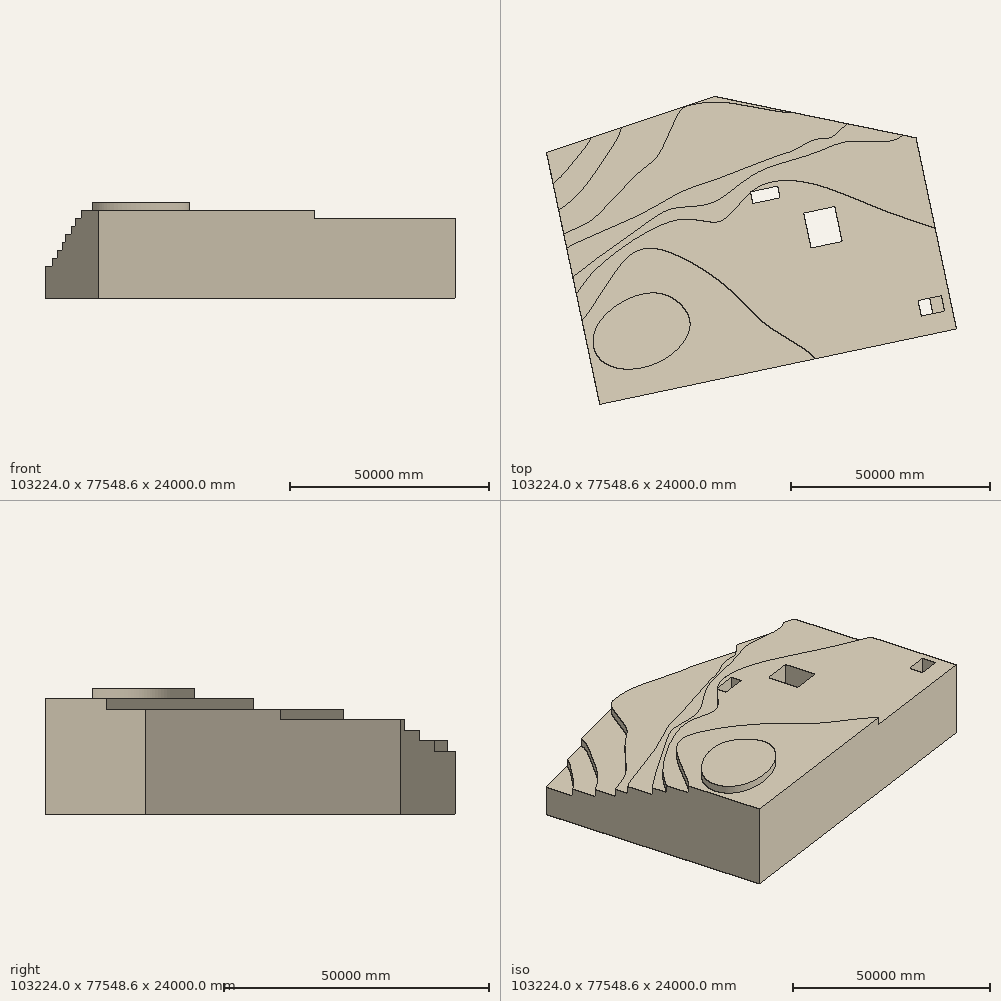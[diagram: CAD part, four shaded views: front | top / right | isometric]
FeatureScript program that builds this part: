
annotation { "Feature Type Name" : "Feature", "Feature Type Description" : "" }
export const myFeature = defineFeature(function(context is Context, id is Id, definition is map)
    precondition{}
    {
        {
            var Q0;
            Q0=qCreatedBy(makeId("Top.planeOp"),FACE);
            var sketch = newSketch(context, id + "F0", { "sketchPlane" : qUnion([Q0])});
            skLineSegment(sketch, "E0.bottom", {"start": v(-42585.65, -35950.06) * mm, "end": v(47226.6, -16950.06) * mm});
            skLineSegment(sketch, "E0.left", {"start": v(-42585.65, -35950.06) * mm, "end": v(-55997.42, 27446.82) * mm});
            skLineSegment(sketch, "E0.right", {"start": v(47226.6, -16950.06) * mm, "end": v(37043.6, 31184.6) * mm});
            skLineSegment(sketch, "E1", {"start": v(-55997.42, 27446.82) * mm, "end": v(-13596.71, 41598.52) * mm});
            skLineSegment(sketch, "E2", {"start": v(-13596.71, 41598.52) * mm, "end": v(37043.6, 31184.6) * mm});
            skSolve(sketch);
        }
        {
            var Q0;
            Q0 = qSketchRegion(id + "F0", true);
            extrude(context, id + "F1", {"entities" : qUnion([Q0]), "oppositeDirection" : true, "depth" : 20000 * mm, "offsetDistance" : 25 * mm});
        }
        {
            var Q0;
            Q0=makeQuery(id+"F1.opExtrude","CAP_FACE",FACE,{"disambiguationData":[OSD([sQuery(id+"F0.wireOp",EDGE,"E0.bottom"),sQuery(id+"F0.wireOp",EDGE,"E0.left"),sQuery(id+"F0.wireOp",EDGE,"E0.right"),sQuery(id+"F0.wireOp",EDGE,"E1"),sQuery(id+"F0.wireOp",EDGE,"E2")])],"isStart":true});
            var sketch = newSketch(context, id + "F2", { "sketchPlane" : qUnion([Q0])});
            skLineSegment(sketch, "E3.bottom", {"start": v(8756.37, 12219.3) * mm, "end": v(16583.14, 13875.07) * mm});
            skLineSegment(sketch, "E3.top", {"start": v(10619.11, 3414.18) * mm, "end": v(18445.89, 5069.95) * mm});
            skLineSegment(sketch, "E3.left", {"start": v(8756.37, 12219.3) * mm, "end": v(10619.11, 3414.18) * mm});
            skLineSegment(sketch, "E3.right", {"start": v(16583.14, 13875.07) * mm, "end": v(18445.89, 5069.95) * mm});
            skSolve(sketch);
        }
        {
            var Q0;
            Q0 = qSketchRegion(id + "F2", true);
            extrude(context, id + "F3", {"entities" : qUnion([Q0]), "operationType" : NewBodyOperationType.REMOVE, "endBound" : BoundingType.THROUGH_ALL, "oppositeDirection" : true, "depth" : 25 * mm, "offsetDistance" : 25 * mm});
        }
        {
            var Q0;
            Q0=makeQuery(id+"F1.opExtrude","CAP_FACE",FACE,{"disambiguationData":[OSD([sQuery(id+"F0.wireOp",EDGE,"E0.bottom"),sQuery(id+"F0.wireOp",EDGE,"E0.left"),sQuery(id+"F0.wireOp",EDGE,"E0.right"),sQuery(id+"F0.wireOp",EDGE,"E1"),sQuery(id+"F0.wireOp",EDGE,"E2")])],"isStart":true});
            var sketch = newSketch(context, id + "F4", { "sketchPlane" : qUnion([Q0])});
            skLineSegment(sketch, "E4.bottom", {"start": v(37537.08, -9800.71) * mm, "end": v(43407.16, -8558.88) * mm});
            skLineSegment(sketch, "E4.top", {"start": v(38364.96, -13714.1) * mm, "end": v(44235.04, -12472.27) * mm});
            skLineSegment(sketch, "E4.left", {"start": v(37537.08, -9800.71) * mm, "end": v(38364.96, -13714.1) * mm});
            skLineSegment(sketch, "E4.right", {"start": v(43407.16, -8558.88) * mm, "end": v(44235.04, -12472.27) * mm});
            skSolve(sketch);
        }
        {
            var Q0;
            Q0 = qSketchRegion(id + "F4", true);
            extrude(context, id + "F5", {"entities" : qUnion([Q0]), "operationType" : NewBodyOperationType.REMOVE, "endBound" : BoundingType.THROUGH_ALL, "oppositeDirection" : true, "depth" : 25 * mm, "offsetDistance" : 25 * mm});
        }
        {
            var Q0;
            Q0=makeQuery(id+"F1.opExtrude","CAP_FACE",FACE,{"disambiguationData":[OSD([sQuery(id+"F0.wireOp",EDGE,"E0.bottom"),sQuery(id+"F0.wireOp",EDGE,"E0.left"),sQuery(id+"F0.wireOp",EDGE,"E0.right"),sQuery(id+"F0.wireOp",EDGE,"E1"),sQuery(id+"F0.wireOp",EDGE,"E2")])],"isStart":true});
            var sketch = newSketch(context, id + "F6", { "sketchPlane" : qUnion([Q0])});
            skLineSegment(sketch, "E5.bottom", {"start": v(-4639.57, 17562.41) * mm, "end": v(2208.86, 19011.22) * mm});
            skLineSegment(sketch, "E5.top", {"start": v(-4018.65, 14627.37) * mm, "end": v(2829.77, 16076.18) * mm});
            skLineSegment(sketch, "E5.left", {"start": v(-4639.57, 17562.41) * mm, "end": v(-4018.65, 14627.37) * mm});
            skLineSegment(sketch, "E5.right", {"start": v(2208.86, 19011.22) * mm, "end": v(2829.77, 16076.18) * mm});
            skSolve(sketch);
        }
        {
            var Q0;
            Q0 = qSketchRegion(id + "F6", true);
            extrude(context, id + "F7", {"entities" : qUnion([Q0]), "operationType" : NewBodyOperationType.REMOVE, "endBound" : BoundingType.THROUGH_ALL, "oppositeDirection" : true, "depth" : 25 * mm, "offsetDistance" : 25 * mm});
        }
        {
            var Q0;
            Q0=makeQuery(id+"F1.opExtrude","CAP_FACE",FACE,{"disambiguationData":[OSD([sQuery(id+"F0.wireOp",EDGE,"E0.bottom"),sQuery(id+"F0.wireOp",EDGE,"E0.left"),sQuery(id+"F0.wireOp",EDGE,"E0.right"),sQuery(id+"F0.wireOp",EDGE,"E1"),sQuery(id+"F0.wireOp",EDGE,"E2")])],"isStart":false});
            var sketch = newSketch(context, id + "F8", { "sketchPlane" : qUnion([Q0])});
            skPoint(sketch, "E6.oppositeSnap0", {"position": v(40472.12, 9179.8) * mm});
            skLineSegment(sketch, "E6.bottom", {"start": v(43407.16, 8558.88) * mm, "end": v(40472.12, 9179.8) * mm});
            skLineSegment(sketch, "E6.top", {"start": v(44235.04, 12472.27) * mm, "end": v(41300, 13093.18) * mm});
            skLineSegment(sketch, "E6.left", {"start": v(43407.16, 8558.88) * mm, "end": v(44235.04, 12472.27) * mm});
            skLineSegment(sketch, "E6.right", {"start": v(40472.12, 9179.8) * mm, "end": v(41300, 13093.18) * mm});
            skSolve(sketch);
        }
        {
            var Q0;
            Q0 = qSketchRegion(id + "F8", true);
            extrude(context, id + "F9", {"entities" : qUnion([Q0]), "operationType" : NewBodyOperationType.ADD, "oppositeDirection" : true, "depth" : 5000 * mm, "offsetDistance" : 25 * mm});
        }
        {
            var Q0;
            Q0=makeQuery(id+"F1.opExtrude","CAP_FACE",FACE,{"disambiguationData":[OSD([sQuery(id+"F0.wireOp",EDGE,"E0.bottom"),sQuery(id+"F0.wireOp",EDGE,"E0.left"),sQuery(id+"F0.wireOp",EDGE,"E0.right"),sQuery(id+"F0.wireOp",EDGE,"E1"),sQuery(id+"F0.wireOp",EDGE,"E2")])],"isStart":true});
            var sketch = newSketch(context, id + "F10", { "sketchPlane" : qUnion([Q0])});
            skFitSpline(sketch, "E7", {"points": [v(-47056.24, -14817.77) * mm, v(-34800.37, 1655.55) * mm, v(-24164.4, 2014.67) * mm, v(-9621.3, -7204.95) * mm, v(-153.95, -16251.36) * mm, v(11663.69, -24473.48) * mm], "startDerivative": vector(45294.7, 43443.74) * mm, "endDerivative": vector(43323.64, -51386.55) * mm});
            skLineSegment(sketch, "E8", {"start": v(-47056.24, -14817.77) * mm, "end": v(-42585.65, -35950.06) * mm});
            skLineSegment(sketch, "E9", {"start": v(-42585.65, -35950.06) * mm, "end": v(11663.69, -24473.48) * mm});
            skSolve(sketch);
        }
        {
            var Q0;
            Q0 = qSketchRegion(id + "F10", true);
            extrude(context, id + "F11", {"entities" : qUnion([Q0]), "operationType" : NewBodyOperationType.ADD, "depth" : 2000 * mm, "offsetDistance" : 25 * mm});
        }
        {
            var Q0;
            Q0=makeQuery(id+"F11.opExtrude","CAP_FACE",FACE,{"disambiguationData":[OSD([sQuery(id+"F10.wireOp",EDGE,"E7"),sQuery(id+"F10.wireOp",EDGE,"E8"),sQuery(id+"F10.wireOp",EDGE,"E9")])],"isStart":false});
            var sketch = newSketch(context, id + "F12", { "sketchPlane" : qUnion([Q0])});
            skFitSpline(sketch, "E10", {"points": [v(-44223.86, -19267.9) * mm, v(-39474.26, -11956.56) * mm, v(-27071.1, -8065.2) * mm, v(-19862.81, -15371.49) * mm, v(-25559.14, -24150.56) * mm, v(-36282.75, -27042.67) * mm, v(-42478.37, -24571.47) * mm, v(-44223.86, -19267.9) * mm]});
            skSolve(sketch);
        }
        {
            var Q0;
            Q0 = qSketchRegion(id + "F12", true);
            extrude(context, id + "F13", {"entities" : qUnion([Q0]), "operationType" : NewBodyOperationType.ADD, "depth" : 2000 * mm, "offsetDistance" : 25 * mm});
        }
        {
            var Q0;
            Q0=makeQuery(id+"F1.opExtrude","CAP_FACE",FACE,{"disambiguationData":[OSD([sQuery(id+"F0.wireOp",EDGE,"E0.bottom"),sQuery(id+"F0.wireOp",EDGE,"E0.left"),sQuery(id+"F0.wireOp",EDGE,"E0.right"),sQuery(id+"F0.wireOp",EDGE,"E1"),sQuery(id+"F0.wireOp",EDGE,"E2")])],"isStart":true});
            var sketch = newSketch(context, id + "F14", { "sketchPlane" : qUnion([Q0])});
            skPoint(sketch, "E11.4.internal.snap0", {"position": v(-2894.94, 18493.67) * mm});
            skPoint(sketch, "E11.5.internal.snap0", {"position": v(2519.32, 17543.7) * mm});
            skFitSpline(sketch, "E11", {"points": [v(-48461.58, -8174.79) * mm, v(-41902.03, -480.55) * mm, v(-22214.21, 10624.74) * mm, v(-12056.5, 10248.96) * mm, v(-3098.95, 18493.67) * mm, v(11165.64, 19577.27) * mm, v(26210.48, 13928.82) * mm, v(41861.9, 8408.7) * mm], "startDerivative": vector(61772.48, 88890.48) * mm, "endDerivative": vector(86929.9, -27804.28) * mm});
            skLineSegment(sketch, "E12", {"start": v(41861.9, 8408.7) * mm, "end": v(37043.6, 31184.6) * mm});
            skLineSegment(sketch, "E13", {"start": v(37043.6, 31184.6) * mm, "end": v(-13596.71, 41598.52) * mm});
            skLineSegment(sketch, "E14", {"start": v(-13596.71, 41598.52) * mm, "end": v(-55997.42, 27446.82) * mm});
            skLineSegment(sketch, "E15", {"start": v(-55997.42, 27446.82) * mm, "end": v(-48461.58, -8174.79) * mm});
            skSolve(sketch);
        }
        {
            var Q0;
            Q0 = qSketchRegion(id + "F14", true);
            extrude(context, id + "F15", {"entities" : qUnion([Q0]), "operationType" : NewBodyOperationType.REMOVE, "oppositeDirection" : true, "depth" : 2000 * mm, "offsetDistance" : 25 * mm});
        }
        {
            var Q0;
            Q0=makeQuery(id+"F15.boolean.opBoolean","COPY",FACE,{"derivedFrom":makeQuery(id+"F15.opExtrude","CAP_FACE",FACE,{"disambiguationData":[OSD([sQuery(id+"F14.wireOp",EDGE,"E11"),sQuery(id+"F14.wireOp",EDGE,"E12"),sQuery(id+"F14.wireOp",EDGE,"E13"),sQuery(id+"F14.wireOp",EDGE,"E14"),sQuery(id+"F14.wireOp",EDGE,"E15")])],"isStart":false})});
            var sketch = newSketch(context, id + "F16", { "sketchPlane" : qUnion([Q0])});
            skFitSpline(sketch, "E16", {"points": [v(-49355.7, -3948.33) * mm, v(-32457.5, 8457.75) * mm, v(-24055.05, 13383.47) * mm, v(-14282.3, 14827.42) * mm, v(-3249.43, 22200.56) * mm, v(10835.35, 27081.4) * mm, v(19620.7, 30197.18) * mm, v(28436.95, 30171.34) * mm, v(33752.23, 31861.46) * mm], "startDerivative": vector(74101.45, 64075.98) * mm, "endDerivative": vector(44716.5, 40997.05) * mm});
            skLineSegment(sketch, "E17", {"start": v(33752.23, 31861.46) * mm, "end": v(-13596.71, 41598.52) * mm});
            skLineSegment(sketch, "E18", {"start": v(-13596.71, 41598.52) * mm, "end": v(-55997.42, 27446.82) * mm});
            skLineSegment(sketch, "E19", {"start": v(-55997.42, 27446.82) * mm, "end": v(-49355.7, -3948.33) * mm});
            skSolve(sketch);
        }
        {
            var Q0;
            Q0 = qSketchRegion(id + "F16", true);
            extrude(context, id + "F17", {"entities" : qUnion([Q0]), "operationType" : NewBodyOperationType.REMOVE, "oppositeDirection" : true, "depth" : 2000 * mm, "offsetDistance" : 25 * mm});
        }
        {
            var Q0;
            Q0=makeQuery(id+"F17.boolean.opBoolean","COPY",FACE,{"derivedFrom":makeQuery(id+"F17.opExtrude","CAP_FACE",FACE,{"disambiguationData":[OSD([sQuery(id+"F16.wireOp",EDGE,"E16"),sQuery(id+"F16.wireOp",EDGE,"E17"),sQuery(id+"F16.wireOp",EDGE,"E18"),sQuery(id+"F16.wireOp",EDGE,"E19")])],"isStart":false})});
            var sketch = newSketch(context, id + "F18", { "sketchPlane" : qUnion([Q0])});
            skFitSpline(sketch, "E20", {"points": [v(-50887.29, 3291.44) * mm, v(-33094.98, 11471.05) * mm, v(-21809.6, 17650.61) * mm, v(-13024.26, 20766.4) * mm, v(934.27, 26244.03) * mm, v(6226, 27997.22) * mm, v(11943.66, 30780.9) * mm, v(15617.92, 31241.33) * mm, v(19924.26, 34705.1) * mm], "startDerivative": vector(49233.01, 38234.62) * mm, "endDerivative": vector(82012.7, 60654.18) * mm});
            skLineSegment(sketch, "E21", {"start": v(19924.26, 34705.1) * mm, "end": v(-13596.71, 41598.52) * mm});
            skLineSegment(sketch, "E22", {"start": v(-13596.71, 41598.52) * mm, "end": v(-55997.42, 27446.82) * mm});
            skLineSegment(sketch, "E23", {"start": v(-55997.42, 27446.82) * mm, "end": v(-50887.29, 3291.44) * mm});
            skSolve(sketch);
        }
        {
            var Q0;
            Q0 = qSketchRegion(id + "F18", true);
            extrude(context, id + "F19", {"entities" : qUnion([Q0]), "operationType" : NewBodyOperationType.REMOVE, "oppositeDirection" : true, "depth" : 2000 * mm, "offsetDistance" : 25 * mm});
        }
        {
            var Q0;
            Q0=makeQuery(id+"F19.boolean.opBoolean","COPY",FACE,{"derivedFrom":makeQuery(id+"F19.opExtrude","CAP_FACE",FACE,{"disambiguationData":[OSD([sQuery(id+"F18.wireOp",EDGE,"E20"),sQuery(id+"F18.wireOp",EDGE,"E21"),sQuery(id+"F18.wireOp",EDGE,"E22"),sQuery(id+"F18.wireOp",EDGE,"E23")])],"isStart":false})});
            var sketch = newSketch(context, id + "F20", { "sketchPlane" : qUnion([Q0])});
            skFitSpline(sketch, "E24", {"points": [v(-51655.15, 6921.1) * mm, v(-43723.24, 11123.79) * mm, v(-32861.45, 22252.85) * mm, v(-27600.62, 27147.68) * mm, v(-22300.18, 37846.38) * mm, v(-18897.05, 39588.45) * mm, v(-10623.6, 40050.83) * mm, v(6096.29, 37548.76) * mm], "startDerivative": vector(91155.04, 46018.1) * mm, "endDerivative": vector(47117.3, 4987.32) * mm});
            skPoint(sketch, "E25", {"position": v(3163.77, 38151.81) * mm});
            skLineSegment(sketch, "E26", {"start": v(6096.29, 37548.76) * mm, "end": v(-13596.71, 41598.52) * mm});
            skLineSegment(sketch, "E27", {"start": v(-13596.71, 41598.52) * mm, "end": v(-55997.42, 27446.82) * mm});
            skLineSegment(sketch, "E28", {"start": v(-55997.42, 27446.82) * mm, "end": v(-51655.15, 6921.1) * mm});
            skSolve(sketch);
        }
        {
            var Q0;
            Q0 = qSketchRegion(id + "F20", true);
            extrude(context, id + "F21", {"entities" : qUnion([Q0]), "operationType" : NewBodyOperationType.REMOVE, "oppositeDirection" : true, "depth" : 2000 * mm, "offsetDistance" : 25 * mm});
        }
        {
            var Q0;
            Q0=makeQuery(id+"F21.boolean.opBoolean","COPY",FACE,{"derivedFrom":makeQuery(id+"F21.opExtrude","CAP_FACE",FACE,{"disambiguationData":[OSD([sQuery(id+"F20.wireOp",EDGE,"E24"),sQuery(id+"F20.wireOp",EDGE,"E26"),sQuery(id+"F20.wireOp",EDGE,"E27"),sQuery(id+"F20.wireOp",EDGE,"E28")])],"isStart":false})});
            var sketch = newSketch(context, id + "F22", { "sketchPlane" : qUnion([Q0])});
            skFitSpline(sketch, "E29", {"points": [v(-52932.17, 12957.5) * mm, v(-46380.59, 18759.12) * mm, v(-41240.12, 26153.15) * mm, v(-37170.31, 33730.57) * mm], "startDerivative": vector(19719.18, 11424.27) * mm, "endDerivative": vector(4027.74, 24326.12) * mm});
            skLineSegment(sketch, "E30", {"start": v(-37170.31, 33730.57) * mm, "end": v(-55997.42, 27446.82) * mm});
            skLineSegment(sketch, "E31", {"start": v(-55997.42, 27446.82) * mm, "end": v(-52932.17, 12957.5) * mm});
            skSolve(sketch);
        }
        {
            var Q0;
            Q0 = qSketchRegion(id + "F22", true);
            extrude(context, id + "F23", {"entities" : qUnion([Q0]), "operationType" : NewBodyOperationType.REMOVE, "oppositeDirection" : true, "depth" : 2000 * mm, "offsetDistance" : 25 * mm});
        }
        {
            var Q0;
            Q0=makeQuery(id+"F23.boolean.opBoolean","COPY",FACE,{"derivedFrom":makeQuery(id+"F23.opExtrude","CAP_FACE",FACE,{"disambiguationData":[OSD([sQuery(id+"F22.wireOp",EDGE,"E29"),sQuery(id+"F22.wireOp",EDGE,"E30"),sQuery(id+"F22.wireOp",EDGE,"E31")])],"isStart":false})});
            var sketch = newSketch(context, id + "F24", { "sketchPlane" : qUnion([Q0])});
            skFitSpline(sketch, "E32", {"points": [v(-54337.5, 19600.48) * mm, v(-49683.26, 24366.99) * mm, v(-44817.63, 31178.2) * mm], "startDerivative": vector(11767.24, 8410.8) * mm, "endDerivative": vector(4113.74, 11552.6) * mm});
            skLineSegment(sketch, "E33", {"start": v(-44817.63, 31178.2) * mm, "end": v(-55997.42, 27446.82) * mm});
            skLineSegment(sketch, "E34", {"start": v(-55997.42, 27446.82) * mm, "end": v(-54337.5, 19600.48) * mm});
            skSolve(sketch);
        }
        {
            var Q0;
            Q0 = qSketchRegion(id + "F24", true);
            extrude(context, id + "F25", {"entities" : qUnion([Q0]), "operationType" : NewBodyOperationType.REMOVE, "oppositeDirection" : true, "depth" : 2000 * mm, "offsetDistance" : 25 * mm});
        }
    });
